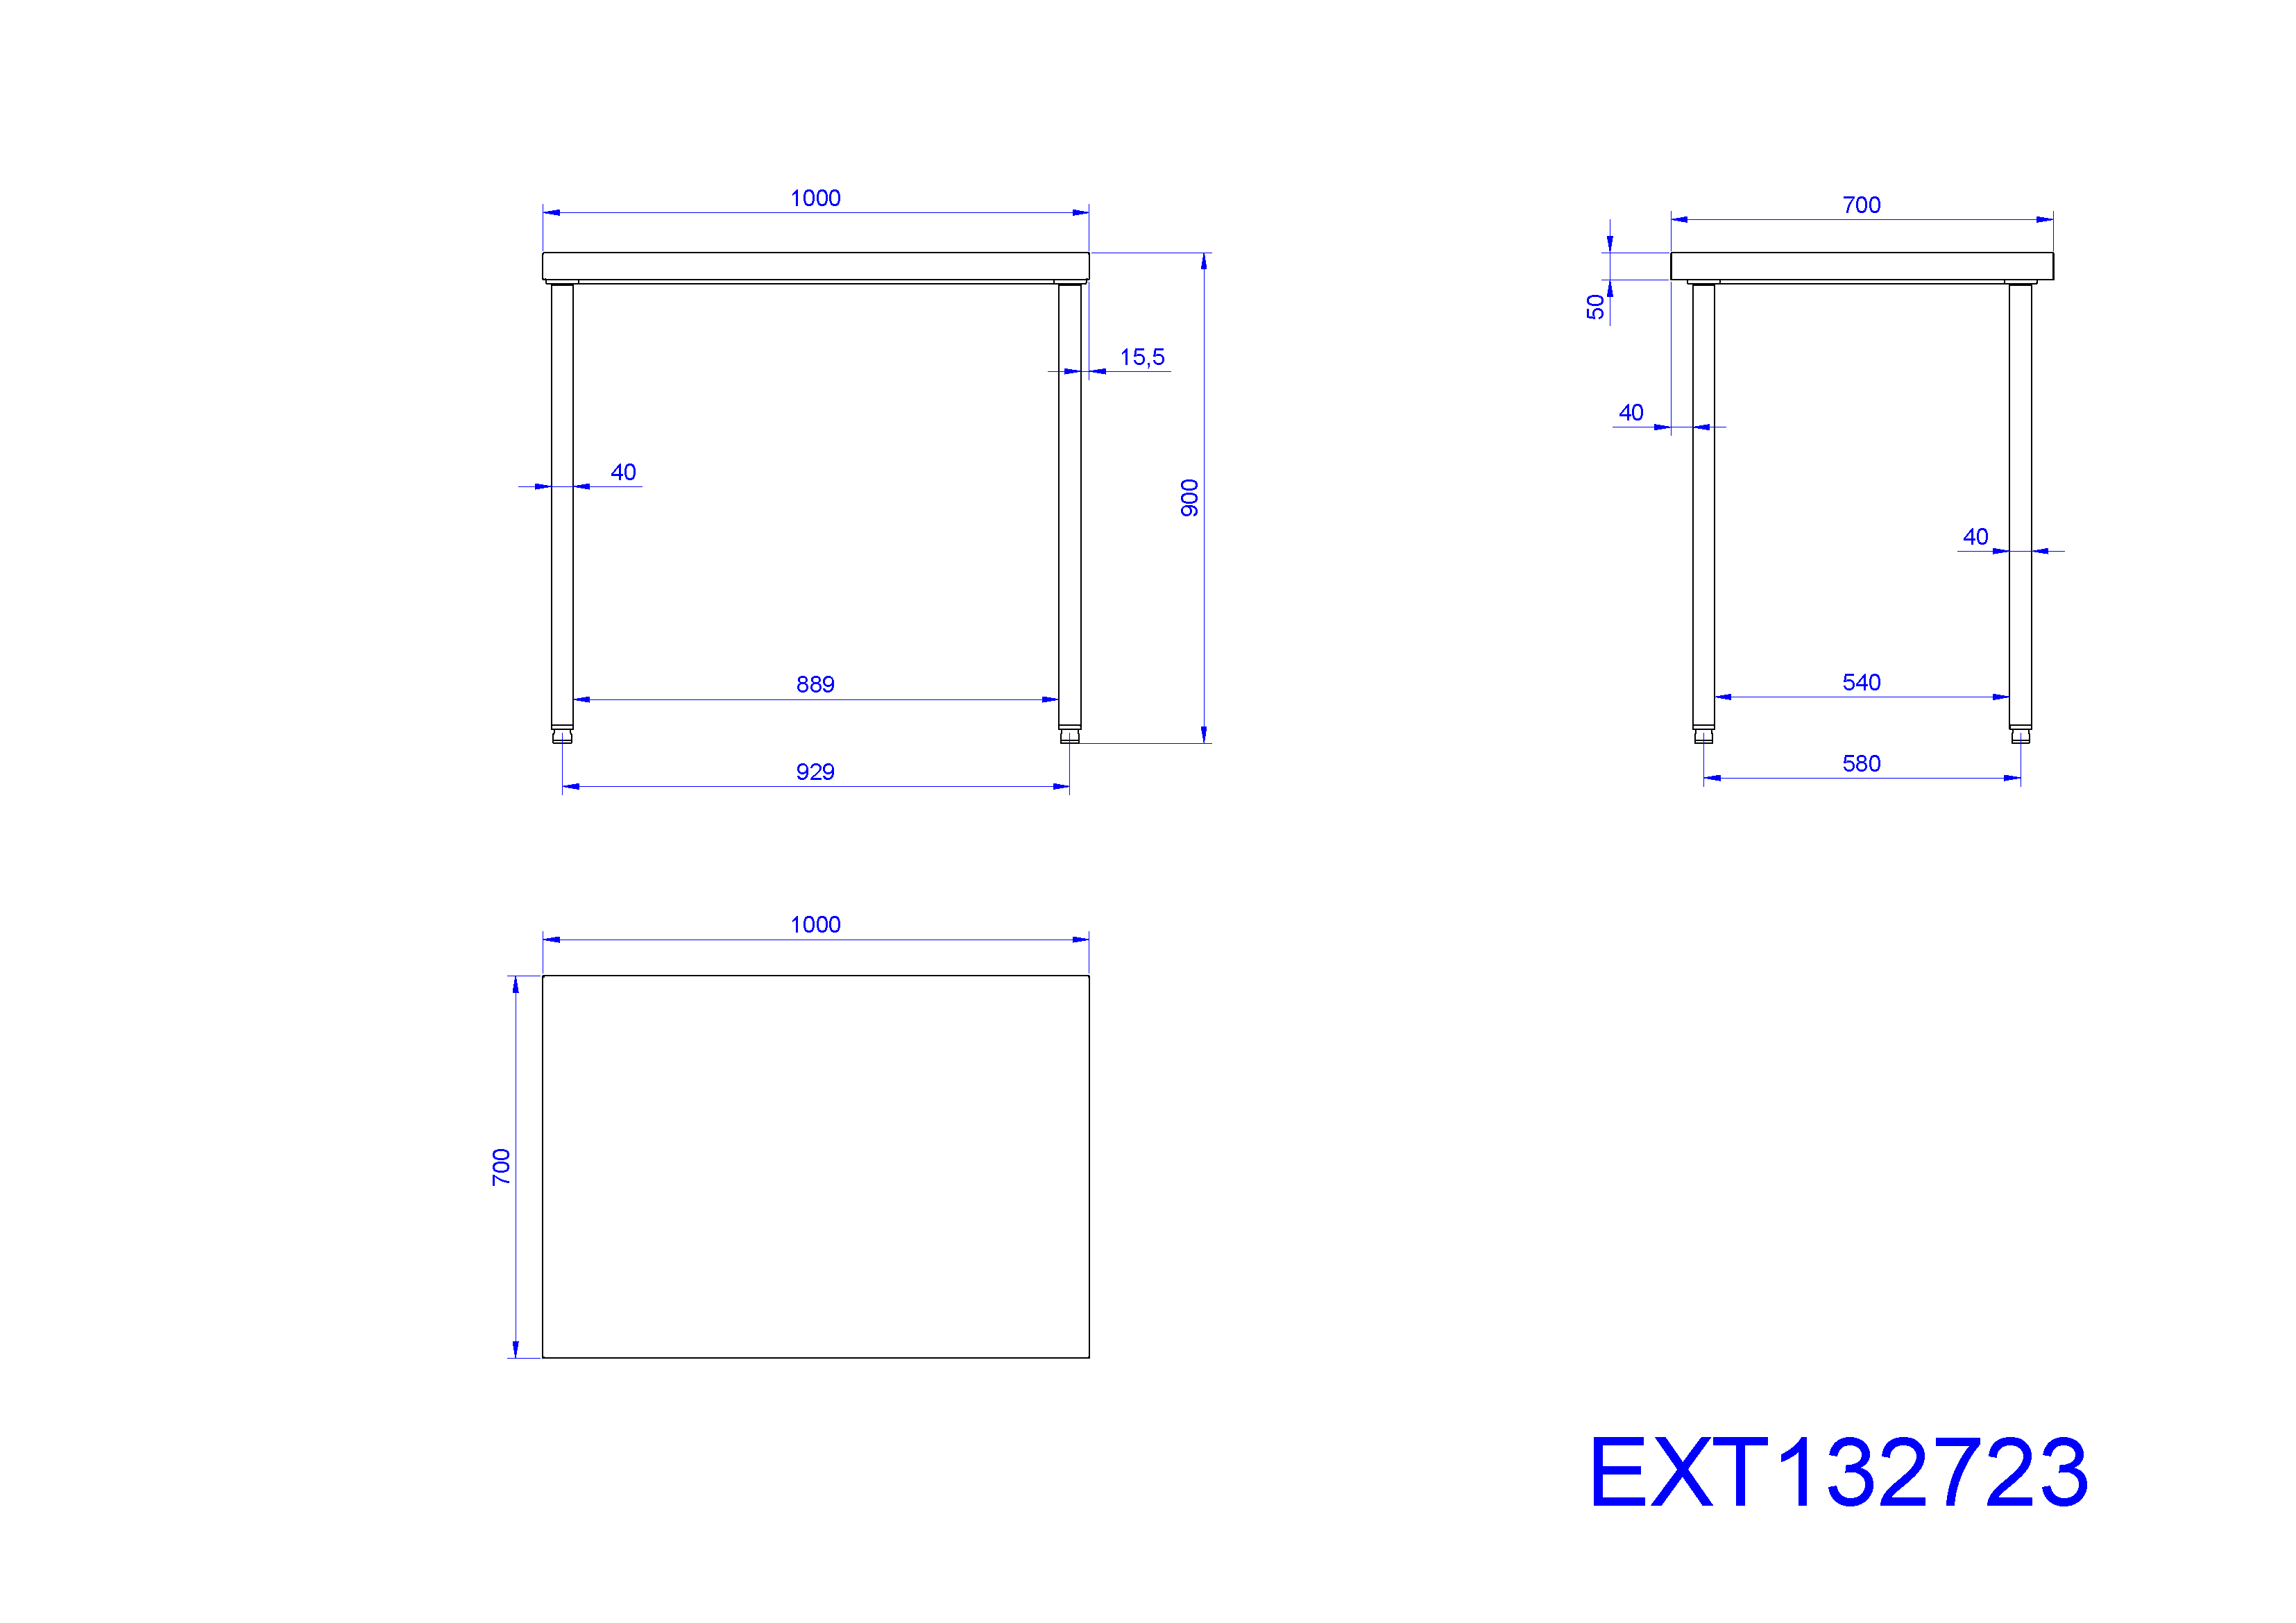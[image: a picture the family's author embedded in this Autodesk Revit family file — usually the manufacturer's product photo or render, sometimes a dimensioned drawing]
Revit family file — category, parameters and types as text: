
# Revit family: QF_ELECTROLUXPROFESSIONAL_132819_MLA1216SXN
name_source: partatom
category: Attrezzature speciali
units: mm (PartAtom-declared; Revit-internal decimal feet)

## family parameters
Basato su piano di lavoro = No
Condiviso = No
Punto di calcolo locali = No
Quota connettore circolare = Usa diametro
Sempre verticale = Sì
Taglio con vuoti quando caricato = No
Tipo di parte = Normale

## types (1)
- Standard
    Accessory = Sì
    Cold Water Size = 0 mm
    Compressed Air Pressure = 0.0 Pa
    Compressed Air Size = 0 mm
    Compressed Air Volume = 0.0 L/s
    Condensate Return Size = 0 mm
    Cycle = 0 Hz
    Depth Actual = 700 mm  [stored 2.29659 ft]
    Descrizione = CUPBOARD SINK 1 BOWL+L/H DRAINER 1200MM
    Direct Waste Size = 51 mm
    Gas Input Pressure = 0
    Gas KW = 0
    Gas Size = 0 mm
    HP = 0 HP
    Height Actual = 1000 mm  [stored 3.28084 ft]
    Hot Water Size = 0 mm
    Item Number = 132819
    Length Actual = 1200 mm
    Modello = MLA1216SXN
    Phase = 0
    Produttore = Electrolux Professional
    Prospetto di default = 0 mm  [stored 0 ft]
    Refrigerant Compressor Remote = Sì
    Refrigeration Liquid Line Size = 0 mm  [stored 0 ft]
    Refrigeration Suction Line Size = 0 mm  [stored 0 ft]
    Steam Consumption per Hour = 0
    Steam Supply Maximum Pressure = 0.0 Pa
    Steam Supply Minimum Pressure = 0.0 Pa
    Steam Supply Size = 0 mm
    URL = https://www.electroluxprofessional.com
    URL Manufacturer = https://www.electroluxprofessional.com
    Volts = 0 V
    Watts = 0 W
    Weight = 55.00 kg

note: source unit labels omitted for Gas Input Pressure — the stored unit's dimension contradicts the parameter name (converter mislabeling)

note: [stored X ft] marks values corroborated as IEEE doubles in the binary element streams (Revit-internal decimal feet)

## geometry (parser evidence)
native form markers: Sweep x6
no freeform markers — native parametric forms only
